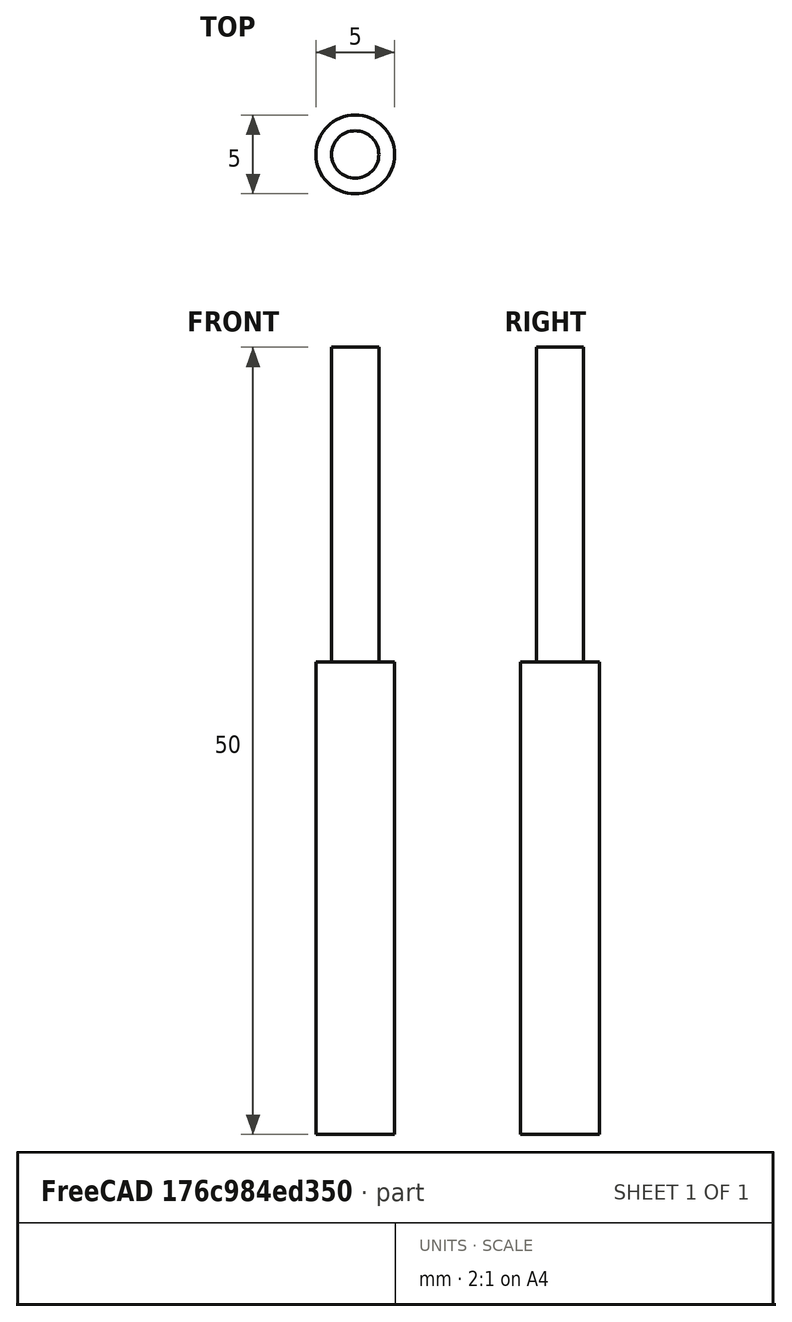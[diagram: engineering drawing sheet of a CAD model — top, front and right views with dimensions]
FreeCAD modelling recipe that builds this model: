
FCSTD DOCUMENT  (FreeCAD 0.19R23587 +23 (Git))
Label: endmill
License: All rights reserved
LicenseURL: http://en.wikipedia.org/wiki/All_rights_reserved
objects: Sketcher::SketchObject×1, PartDesign::Revolution×1, App::FeaturePython×1, PartDesign::Body×1
note: 4 computed .brp shape members not serialized (recipe doc carries the construction recipe); baked Part::Feature solids carry a one-line shape summary decoded from their .brp

FEATURE [Sketcher::SketchObject] Sketch
  MapMode = 5
  Placement = pos=(0,0,0) rot=(1,0,0;1.5708rad)
  Support = -> [XZ_Plane]
  expr: Constraints[18] = <<Attributes>>.CuttingEdgeHeight
  expr: Constraints[16] = <<Attributes>>.ShankDiameter
  expr: Constraints[10] = <<Attributes>>.Length
  expr: Constraints[9] = <<Attributes>>.Diameter
  sketch-geometry (8):
    g0: LineSegment StartX=0 StartY=50 StartZ=0 EndX=0 EndY=0 EndZ=0
    g1: LineSegment StartX=0 StartY=0 StartZ=0 EndX=2.5 EndY=0 EndZ=0
    g2: LineSegment StartX=2.5 StartY=0 StartZ=0 EndX=2.5 EndY=30 EndZ=0
    g3: LineSegment StartX=1.5 StartY=50 StartZ=0 EndX=0 EndY=50 EndZ=0
    g4: LineSegment StartX=2.5 StartY=0 StartZ=0 EndX=-2.5 EndY=0 EndZ=0
    g5: LineSegment StartX=1.5 StartY=29.99 StartZ=0 EndX=2.5 EndY=30 EndZ=0
    g6: LineSegment StartX=1.5 StartY=50 StartZ=0 EndX=1.5 EndY=29.99 EndZ=0
    g7: LineSegment StartX=-1.5 StartY=50 StartZ=0 EndX=1.5 EndY=50 EndZ=0
  constraints (21):
    c: Vertical(g0)
    c: Coincident(g0,g1)
    c: Horizontal(g1)
    c: Coincident(g1,g2)
    c: Vertical(g2)
    c: Horizontal(g3)
    c: Coincident(g0,g3)
    c: Coincident(g4,g1)
    c: Symmetric(g1,g4,g0)
    c: DistanceX(g4,g4) = 5
    c: DistanceY(g2,g3) = 50
    c: Coincident(g2,g5)
    c: Vertical(g6)
    c: Coincident(g3,g6)
    c: Symmetric(g7,g7,g0)
    c: Coincident(g7,g3)
    c: DistanceX(g7,g7) = 3
    c: Coincident(g5,g6)
    c: DistanceY(g2) = 30
    c: Coincident(g0,g-1)
    c: DistanceY(g5,g2) = 0.01
FEATURE [PartDesign::Revolution] Revolution
  AllowMultiFace = false
  Angle = 360
  Axis = (0,-2e-16,1)
  Base = (0,0,0)
  Placement = pos=(0,0,0) rot=(1,0,0;1.5708rad)
  Profile = -> Sketch
  ReferenceAxis = -> Sketch [V_Axis]
  Reversed = true
FEATURE [App::FeaturePython] PropertyBag  label="Attributes"  # WARN: FeaturePython — macro-defined, semantics opaque (R4)
  Chipload = 3
  CustomPropertyGroups = Geometry | Details | Extra | Shape
  CuttingEdgeHeight = 30
  Diameter = 5
  Flutes = 3
  Length = 50
  Material = 1
  ShankDiameter = 3
FEATURE [PartDesign::Body] Body  label="Endmill"
  Group = -> [Sketch,Revolution,PropertyBag]
  Origin = -> Origin
  Tip = -> Revolution
